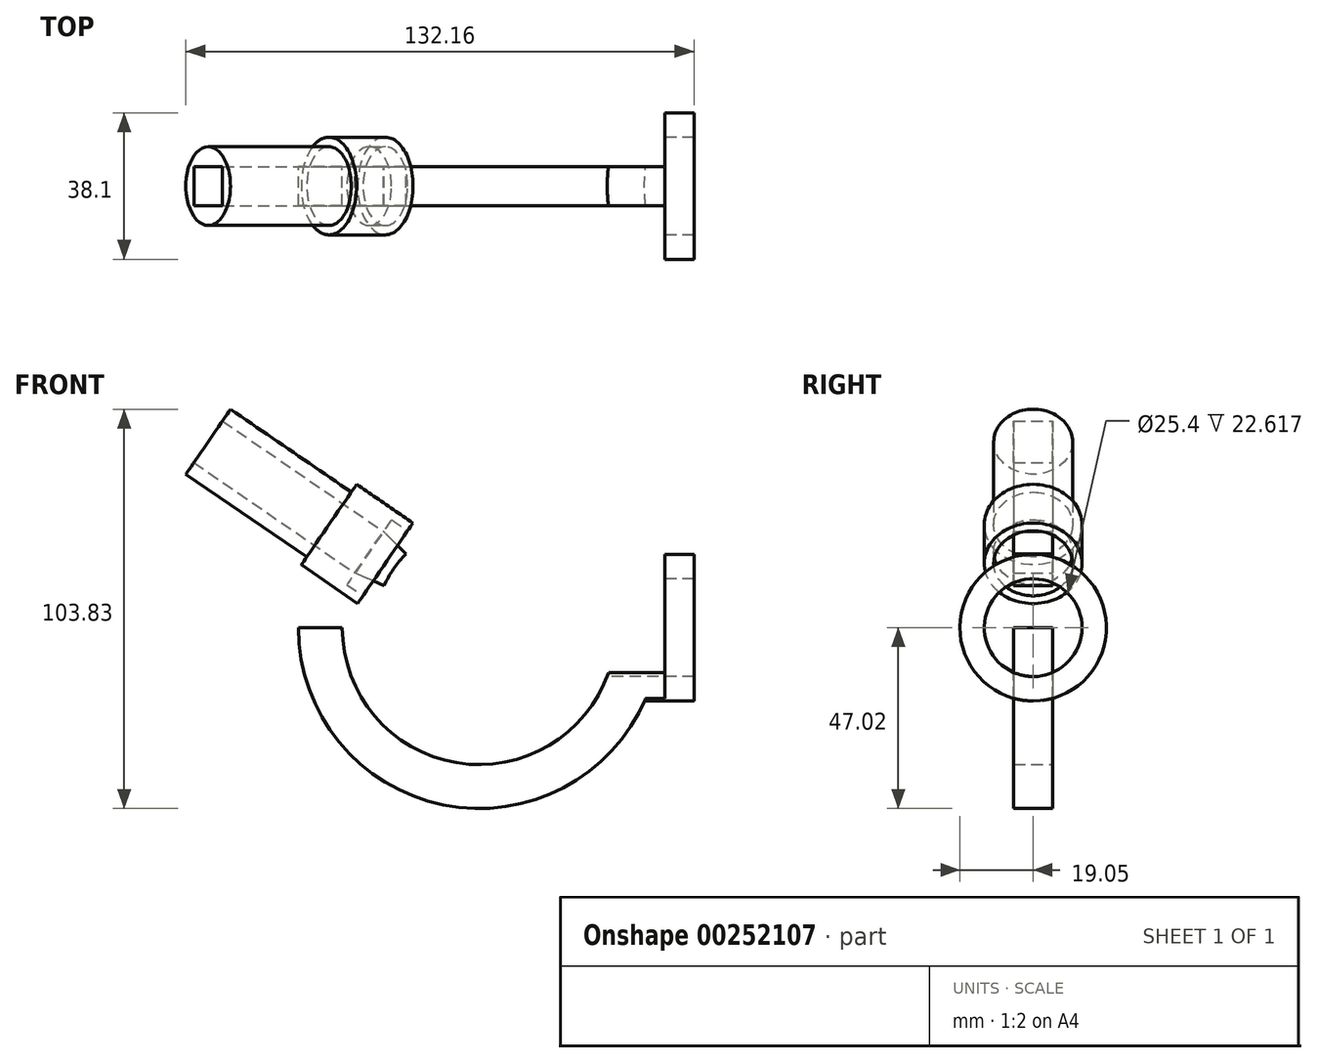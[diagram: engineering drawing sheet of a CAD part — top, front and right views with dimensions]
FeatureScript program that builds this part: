
annotation { "Feature Type Name" : "Feature", "Feature Type Description" : "" }
export const myFeature = defineFeature(function(context is Context, id is Id, definition is map)
    precondition{}
    {
        {
            var Q0;
            Q0=qCreatedBy(makeId("Front.planeOp"),FACE);
            var sketch = newSketch(context, id + "F0", { "sketchPlane" : qUnion([Q0])});
            skArc(sketch, "E0", {"start": v(-35.6, 0) * mm, "mid": v(0, -35.6) * mm, "end": v(35.6, 0) * mm});
            skArc(sketch, "E1", {"start": v(-47.02, 0) * mm, "mid": v(0, -47.02) * mm, "end": v(47.02, 0) * mm});
            skLineSegment(sketch, "E2", {"start": v(35.6, 0) * mm, "end": v(47.02, 0) * mm});
            skLineSegment(sketch, "E3", {"start": v(-35.6, 0) * mm, "end": v(-47.02, 0) * mm});
            skArc(sketch, "E4", {"start": v(-19.04, 19.16) * mm, "mid": v(-22.27, 15.28) * mm, "end": v(-24.73, 10.88) * mm});
            skLineSegment(sketch, "E5", {"start": v(0, 0) * mm, "end": v(-32.3, 14.21) * mm, "construction": true});
            skLineSegment(sketch, "E6", {"start": v(0, 0) * mm, "end": v(-24.88, 25.03) * mm, "construction": true});
            skLineSegment(sketch, "E7", {"start": v(-19.04, 19.16) * mm, "end": v(-24.88, 25.03) * mm});
            skLineSegment(sketch, "E8", {"start": v(-24.73, 10.88) * mm, "end": v(-32.3, 14.21) * mm});
            skLineSegment(sketch, "E9", {"start": v(-32.3, 14.21) * mm, "end": v(-24.88, 25.03) * mm});
            skSolve(sketch);
        }
        {
            var Q0;
            Q0=makeQuery(id+"F0.imprint","IMPRINT",FACE,{"disambiguationData":[TD([[makeQuery(id+"F0.imprint","IMPRINT",EDGE,{"derivedFrom":sQuery(id+"F0.wireOp",EDGE,"E4")}),-1.0]])]});
            extrude(context, id + "F1", {"entities" : qUnion([Q0]), "depth" : 5.08 * mm, "hasSecondDirection" : true, "secondDirectionOppositeDirection" : true, "secondDirectionDepth" : 5.08 * mm});
        }
        {
            var Q0;
            Q0=makeQuery(id+"F0.imprint","IMPRINT",FACE,{"disambiguationData":[TD([[makeQuery(id+"F0.imprint","IMPRINT",EDGE,{"derivedFrom":sQuery(id+"F0.wireOp",EDGE,"E0")}),-1.0]])]});
            extrude(context, id + "F2", {"entities" : qUnion([Q0]), "depth" : 5.08 * mm, "hasSecondDirection" : true, "secondDirectionOppositeDirection" : true, "secondDirectionDepth" : 5.08 * mm});
        }
        {
            var Q0;
            Q0=makeQuery(id+"F1.opExtrude","SWEPT_FACE",FACE,{"disambiguationData":[OSD([sQuery(id+"F0.wireOp",EDGE,"E9")])]});
            var sketch = newSketch(context, id + "F3", { "sketchPlane" : qUnion([Q0])});
            skCircle(sketch, "E10", {"center": v(0, 0) * mm, "radius": 12.7 * mm});
            skCircle(sketch, "E11", {"center": v(0, 0) * mm, "radius": 10.25 * mm});
            skSolve(sketch);
        }
        {
            var Q0;
            Q0=makeQuery(id+"F3.imprint","IMPRINT",FACE,{"disambiguationData":[TD([[makeQuery(id+"F3.imprint","IMPRINT",EDGE,{"derivedFrom":sQuery(id+"F3.wireOp",EDGE,"E10")}),1.0]])]});
            extrude(context, id + "F4", {"entities" : qUnion([Q0]), "operationType" : NewBodyOperationType.ADD, "depth" : 12.7 * mm, "hasSecondDirection" : true, "secondDirectionOppositeDirection" : true, "secondDirectionDepth" : 5.08 * mm});
        }
        {
            var Q0;
            Q0=qCreatedBy(makeId("Right.planeOp"),FACE);
            var sketch = newSketch(context, id + "F5", { "sketchPlane" : qUnion([Q0])});
            skCircle(sketch, "E12", {"center": v(0, 0) * mm, "radius": 19.05 * mm});
            skCircle(sketch, "E13", {"center": v(0, 0) * mm, "radius": 12.7 * mm});
            skLineSegment(sketch, "E14", {"start": v(5.08, -18.36) * mm, "end": v(5.08, -11.64) * mm});
            skLineSegment(sketch, "E15", {"start": v(-5.08, -18.36) * mm, "end": v(-5.08, -11.64) * mm});
            skSolve(sketch);
        }
        {
            var Q0;
            Q0=makeQuery(id+"F5.imprint","IMPRINT",FACE,{"disambiguationData":[TD([[makeQuery(id+"F5.imprint","IMPRINT",EDGE,{"derivedFrom":sQuery(id+"F5.wireOp",EDGE,"E12")}),1.0]])]});
            var Q1;
            Q1=makeQuery(id+"F2.opExtrude","SWEPT_BODY",BODY,{"disambiguationData":[OSD([sQuery(id+"F0.wireOp",EDGE,"E0"),sQuery(id+"F0.wireOp",EDGE,"E1"),sQuery(id+"F0.wireOp",EDGE,"E2"),sQuery(id+"F0.wireOp",EDGE,"E3")])]});
            var Q2;
            Q2=makeQuery(id+"F2.opExtrude","SWEPT_BODY",BODY,{"disambiguationData":[OSD([sQuery(id+"F0.wireOp",EDGE,"E0"),sQuery(id+"F0.wireOp",EDGE,"E1"),sQuery(id+"F0.wireOp",EDGE,"E2"),sQuery(id+"F0.wireOp",EDGE,"E3")])]});
            extrude(context, id + "F6", {"entities" : qUnion([Q0]), "operationType" : NewBodyOperationType.ADD, "endBoundEntityBody" : qUnion([Q1]), "depth" : 55.88 * mm, "hasSecondDirection" : true, "secondDirectionOppositeDirection" : false, "secondDirectionBoundEntityBody" : qUnion([Q2]), "secondDirectionDepth" : 38.1 * mm});
        }
        {
            var Q0;
            {var subQ0=sQuery(id+"F3.wireOp",EDGE,"E11");var subQ1=sQuery(id+"F0.wireOp",EDGE,"E9");var subQ2=makeQuery(id+"F1.opExtrude","SWEPT_EDGE",EDGE,{"disambiguationData":[OSD([sQuery(id+"F0.wireOp",EDGE,"E7"),subQ1])]});var subQ3=makeQuery(id+"F3.imprint","INTERSECT",VERTEX,{"disambiguationData":[OD(0.0)],"derivedFrom":[subQ2,subQ0]});Q0=makeQuery(id+"F3.imprint","IMPRINT",FACE,{"disambiguationData":[TD([[makeQuery(id+"F3.imprint","IMPRINT",EDGE,{"disambiguationData":[TD([[subQ3,-1.0]])],"derivedFrom":subQ0}),1.0]])]});}
            var Q1;
            {var subQ0=sQuery(id+"F3.wireOp",EDGE,"E11");var subQ1=makeQuery(id+"F1.opExtrude","SWEPT_EDGE",EDGE,{"disambiguationData":[OSD([sQuery(id+"F0.wireOp",EDGE,"E7"),sQuery(id+"F0.wireOp",EDGE,"E9")])]});var subQ2=makeQuery(id+"F3.imprint","INTERSECT",VERTEX,{"disambiguationData":[OD(0.0)],"derivedFrom":[subQ1,subQ0]});Q1=makeQuery(id+"F3.imprint","IMPRINT",FACE,{"disambiguationData":[TD([[makeQuery(id+"F3.imprint","IMPRINT",EDGE,{"disambiguationData":[TD([[subQ2,1.0]])],"derivedFrom":subQ0}),1.0]])]});}
            var Q2;
            {var subQ0=sQuery(id+"F3.wireOp",EDGE,"E11");var subQ1=makeQuery(id+"F1.opExtrude","SWEPT_EDGE",EDGE,{"disambiguationData":[OSD([sQuery(id+"F0.wireOp",EDGE,"E8"),sQuery(id+"F0.wireOp",EDGE,"E9")])]});var subQ2=makeQuery(id+"F3.imprint","INTERSECT",VERTEX,{"disambiguationData":[OD(0.0)],"derivedFrom":[subQ1,subQ0]});Q2=makeQuery(id+"F3.imprint","IMPRINT",FACE,{"disambiguationData":[TD([[makeQuery(id+"F3.imprint","IMPRINT",EDGE,{"disambiguationData":[TD([[subQ2,-1.0]])],"derivedFrom":subQ0}),1.0]])]});}
            extrude(context, id + "F7", {"entities" : qUnion([Q0, Q1, Q2]), "operationType" : NewBodyOperationType.ADD, "depth" : 50.8 * mm});
        }
        {
            var Q0;
            Q0=makeQuery(id+"F5.imprint","IMPRINT",FACE,{"disambiguationData":[TD([[makeQuery(id+"F5.imprint","IMPRINT",EDGE,{"derivedFrom":sQuery(id+"F5.wireOp",EDGE,"E13")}),1.0]])]});
            var Q1;
            {var subQ0=sQuery(id+"F5.wireOp",EDGE,"E14");Q1=makeQuery(id+"F5.imprint","IMPRINT",FACE,{"disambiguationData":[TD([[makeQuery(id+"F5.imprint","IMPRINT",EDGE,{"derivedFrom":subQ0}),-1.0]])]});}
            extrude(context, id + "F8", {"entities" : qUnion([Q0, Q1]), "operationType" : NewBodyOperationType.REMOVE, "depth" : 48.26 * mm, "hasSecondDirection" : true, "secondDirectionOppositeDirection" : false, "secondDirectionDepth" : 30.48 * mm});
        }
    });
